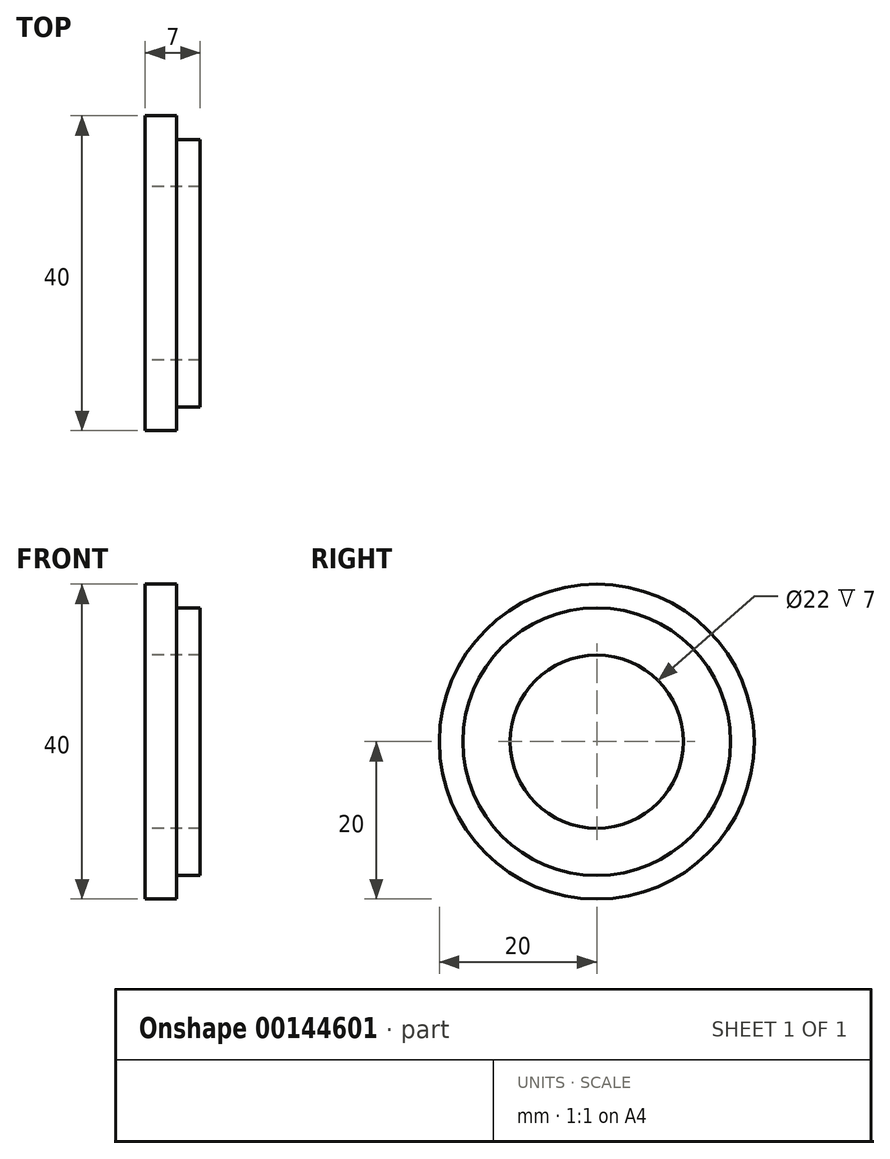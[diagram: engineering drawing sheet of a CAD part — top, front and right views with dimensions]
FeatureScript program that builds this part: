
annotation { "Feature Type Name" : "Feature", "Feature Type Description" : "" }
export const myFeature = defineFeature(function(context is Context, id is Id, definition is map)
    precondition{}
    {
        {
            var Q0;
            Q0=qCreatedBy(makeId("Front.planeOp"),FACE);
            var sketch = newSketch(context, id + "F0", { "sketchPlane" : qUnion([Q0])});
            skLineSegment(sketch, "E0", {"start": v(0, 20) * mm, "end": v(4, 20) * mm});
            skLineSegment(sketch, "E1", {"start": v(4, 20) * mm, "end": v(4, 17) * mm});
            skLineSegment(sketch, "E2", {"start": v(4, 17) * mm, "end": v(7, 17) * mm});
            skLineSegment(sketch, "E3", {"start": v(7, 11.2) * mm, "end": v(7, 17) * mm, "construction": true});
            skLineSegment(sketch, "E4", {"start": v(7, 11) * mm, "end": v(0, 11) * mm});
            skLineSegment(sketch, "E5", {"start": v(0, 20) * mm, "end": v(0, 11) * mm});
            skLineSegment(sketch, "E6", {"start": v(7, 17) * mm, "end": v(7, 11) * mm});
            skLineSegment(sketch, "E7", {"start": v(-10.85, 0) * mm, "end": v(18.5, 0) * mm, "construction": true});
            skSolve(sketch);
        }
        {
            var Q0;
            Q0=makeQuery(id+"F0.imprint","IMPRINT",FACE,{"disambiguationData":[TD([[makeQuery(id+"F0.imprint","IMPRINT",EDGE,{"derivedFrom":sQuery(id+"F0.wireOp",EDGE,"E0")}),-1.0]])]});
            var Q1;
            Q1=sQuery(id+"F0.wireOp",EDGE,"E7");
            revolve(context, id + "F1", {"entities" : qUnion([Q0]), "axis" : qUnion([Q1]), "revolveType" : RevolveType.FULL});
        }
    });
